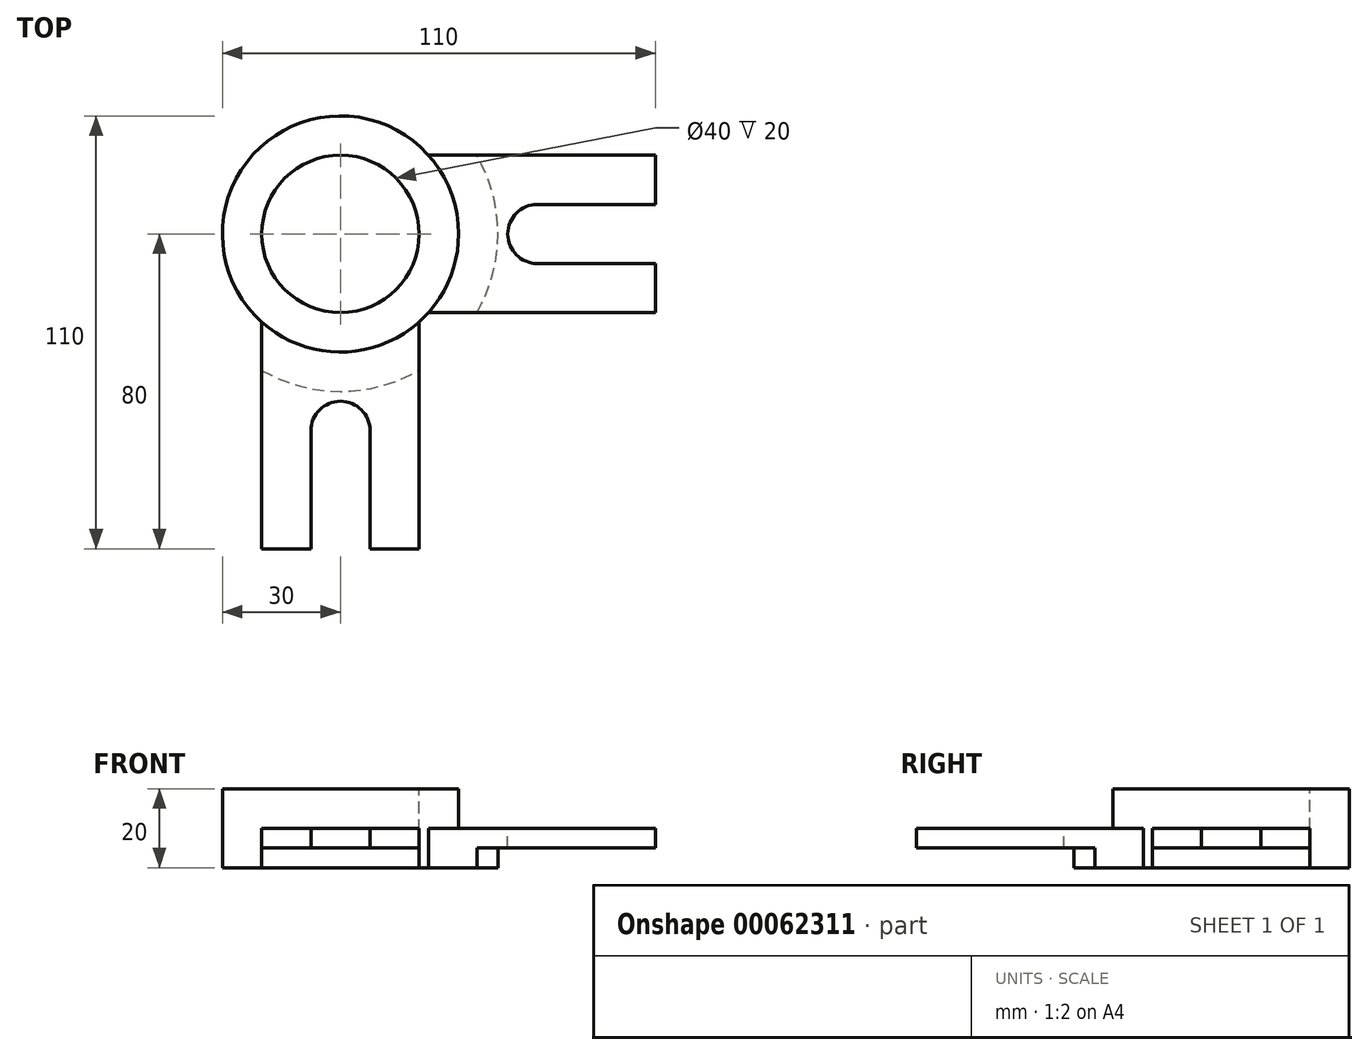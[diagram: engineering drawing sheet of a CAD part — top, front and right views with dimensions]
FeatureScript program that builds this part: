
annotation { "Feature Type Name" : "Feature", "Feature Type Description" : "" }
export const myFeature = defineFeature(function(context is Context, id is Id, definition is map)
    precondition{}
    {
        {
            var Q0;
            Q0=qCreatedBy(makeId("Top.planeOp"),FACE);
            var sketch = newSketch(context, id + "F0", { "sketchPlane" : qUnion([Q0])});
            skCircle(sketch, "E0", {"center": v(0, 0) * mm, "radius": 30 * mm});
            skSolve(sketch);
        }
        {
            var Q0;
            Q0=makeQuery(id+"F0.imprint","IMPRINT",FACE,{"disambiguationData":[TD([[makeQuery(id+"F0.imprint","IMPRINT",EDGE,{"derivedFrom":sQuery(id+"F0.wireOp",EDGE,"E0")}),1.0]])]});
            extrude(context, id + "F1", {"entities" : qUnion([Q0]), "depth" : 20 * mm});
        }
        {
            var Q0;
            Q0=qCreatedBy(makeId("Top.planeOp"),FACE);
            var sketch = newSketch(context, id + "F2", { "sketchPlane" : qUnion([Q0])});
            skLineSegment(sketch, "E1.bottom", {"start": v(22.36, -20) * mm, "end": v(80, -20) * mm});
            skLineSegment(sketch, "E1.top", {"start": v(22.36, 20) * mm, "end": v(80, 20) * mm});
            skLineSegment(sketch, "E1.right", {"start": v(80, -20) * mm, "end": v(80, 20) * mm});
            skLineSegment(sketch, "E2.top", {"start": v(-20, -80) * mm, "end": v(20, -80) * mm});
            skLineSegment(sketch, "E2.left", {"start": v(-20, -22.36) * mm, "end": v(-20, -80) * mm});
            skArc(sketch, "E3", {"start": v(-20, -22.36) * mm, "mid": v(21.21, -21.21) * mm, "end": v(22.36, 20) * mm});
            skLineSegment(sketch, "E4.trimOffspring", {"start": v(20, -22.36) * mm, "end": v(20, -80) * mm});
            skSolve(sketch);
        }
        {
            var Q0;
            {var subQ0=sQuery(id+"F2.wireOp",EDGE,"E1.bottom");Q0=makeQuery(id+"F2.imprint","IMPRINT",FACE,{"disambiguationData":[TD([[makeQuery(id+"F2.imprint","IMPRINT",EDGE,{"derivedFrom":subQ0}),1.0]])]});}
            var Q1;
            Q1=makeQuery(id+"F2.imprint","IMPRINT",FACE,{"disambiguationData":[TD([[makeQuery(id+"F2.imprint","IMPRINT",EDGE,{"derivedFrom":sQuery(id+"F2.wireOp",EDGE,"E2.top")}),1.0]])]});
            extrude(context, id + "F3", {"entities" : qUnion([Q0, Q1]), "operationType" : NewBodyOperationType.ADD, "depth" : 10 * mm});
        }
        {
            var Q0;
            Q0=makeQuery(id+"F3.opExtrude","CAP_FACE",FACE,{"disambiguationData":[OSD([sQuery(id+"F2.wireOp",EDGE,"E2.top"),sQuery(id+"F2.wireOp",EDGE,"E2.left"),sQuery(id+"F2.wireOp",EDGE,"E3"),sQuery(id+"F2.wireOp",EDGE,"E4.trimOffspring")])],"isStart":false});
            var sketch = newSketch(context, id + "F4", { "sketchPlane" : qUnion([Q0])});
            skArc(sketch, "E5", {"start": v(7.5, -50) * mm, "mid": v(0, -42.5) * mm, "end": v(-7.5, -50) * mm});
            skPoint(sketch, "E5.centerSnap0", {"position": v(0, -80) * mm});
            skLineSegment(sketch, "E6.3", {"start": v(-25, -85) * mm, "end": v(25, -85) * mm});
            skLineSegment(sketch, "E7.0", {"start": v(7.5, -50) * mm, "end": v(7.5, -80) * mm});
            skLineSegment(sketch, "E8.0", {"start": v(-7.5, -50) * mm, "end": v(-7.5, -80) * mm});
            skLineSegment(sketch, "E9", {"start": v(-7.5, -80) * mm, "end": v(7.5, -80) * mm});
            skSolve(sketch);
        }
        {
            var Q0;
            Q0=makeQuery(id+"F4.imprint","IMPRINT",FACE,{"disambiguationData":[TD([[makeQuery(id+"F4.imprint","IMPRINT",EDGE,{"derivedFrom":sQuery(id+"F4.wireOp",EDGE,"E5")}),1.0]])]});
            extrude(context, id + "F5", {"entities" : qUnion([Q0]), "operationType" : NewBodyOperationType.REMOVE, "oppositeDirection" : true, "depth" : 25 * mm});
        }
        {
            var Q0;
            Q0=makeQuery(id+"F3.opExtrude","CAP_FACE",FACE,{"disambiguationData":[OSD([sQuery(id+"F2.wireOp",EDGE,"E1.bottom"),sQuery(id+"F2.wireOp",EDGE,"E1.top"),sQuery(id+"F2.wireOp",EDGE,"E1.right"),sQuery(id+"F2.wireOp",EDGE,"E3")])],"isStart":false});
            var sketch = newSketch(context, id + "F6", { "sketchPlane" : qUnion([Q0])});
            skArc(sketch, "E10", {"start": v(50, 7.5) * mm, "mid": v(42.5, 0) * mm, "end": v(50, -7.5) * mm});
            skLineSegment(sketch, "E11.0", {"start": v(50, 7.5) * mm, "end": v(80, 7.5) * mm});
            skLineSegment(sketch, "E12.0", {"start": v(50, -7.5) * mm, "end": v(80, -7.5) * mm});
            skLineSegment(sketch, "E13", {"start": v(80, 7.5) * mm, "end": v(80, -7.5) * mm});
            skSolve(sketch);
        }
        {
            var Q0;
            Q0=makeQuery(id+"F6.imprint","IMPRINT",FACE,{"disambiguationData":[TD([[makeQuery(id+"F6.imprint","IMPRINT",EDGE,{"derivedFrom":sQuery(id+"F6.wireOp",EDGE,"E10")}),1.0]])]});
            extrude(context, id + "F7", {"entities" : qUnion([Q0]), "operationType" : NewBodyOperationType.REMOVE, "oppositeDirection" : true, "depth" : 10 * mm});
        }
        {
            var Q0;
            Q0=qCreatedBy(makeId("Top.planeOp"),FACE);
            var sketch = newSketch(context, id + "F8", { "sketchPlane" : qUnion([Q0])});
            skArc(sketch, "E14", {"start": v(-20, -34.64) * mm, "mid": v(0, -40) * mm, "end": v(20, -34.64) * mm});
            skLineSegment(sketch, "E15.top", {"start": v(-20, -80) * mm, "end": v(20, -80) * mm});
            skLineSegment(sketch, "E15.left", {"start": v(-20, -34.64) * mm, "end": v(-20, -80) * mm});
            skLineSegment(sketch, "E15.right", {"start": v(20, -34.64) * mm, "end": v(20, -80) * mm});
            skLineSegment(sketch, "E16.bottom", {"start": v(34.45, -20) * mm, "end": v(80, -20) * mm});
            skLineSegment(sketch, "E16.top", {"start": v(34.41, 20) * mm, "end": v(80, 20) * mm});
            skLineSegment(sketch, "E16.right", {"start": v(80, -20) * mm, "end": v(80, 20) * mm});
            skArc(sketch, "E17.trimOffspring", {"start": v(34.64, -20) * mm, "mid": v(40, 0) * mm, "end": v(34.64, 20) * mm});
            skSolve(sketch);
        }
        {
            var Q0;
            Q0=makeQuery(id+"F8.imprint","IMPRINT",FACE,{"disambiguationData":[TD([[makeQuery(id+"F8.imprint","IMPRINT",EDGE,{"derivedFrom":sQuery(id+"F8.wireOp",EDGE,"E14")}),-1.0]])]});
            var Q1;
            {var subQ0=sQuery(id+"F8.wireOp",EDGE,"E16.right");Q1=makeQuery(id+"F8.imprint","IMPRINT",FACE,{"disambiguationData":[TD([[makeQuery(id+"F8.imprint","IMPRINT",EDGE,{"derivedFrom":subQ0}),1.0]])]});}
            extrude(context, id + "F9", {"entities" : qUnion([Q0, Q1]), "operationType" : NewBodyOperationType.REMOVE, "depth" : 5 * mm});
        }
        {
            var Q0;
            Q0=makeQuery(id+"F1.opExtrude","CAP_FACE",FACE,{"disambiguationData":[OSD([sQuery(id+"F0.wireOp",EDGE,"E0")])],"isStart":false});
            var sketch = newSketch(context, id + "F10", { "sketchPlane" : qUnion([Q0])});
            skCircle(sketch, "E18", {"center": v(0, 0) * mm, "radius": 20 * mm});
            skSolve(sketch);
        }
        {
            var Q0;
            Q0=makeQuery(id+"F10.imprint","IMPRINT",FACE,{"disambiguationData":[TD([[makeQuery(id+"F10.imprint","IMPRINT",EDGE,{"derivedFrom":sQuery(id+"F10.wireOp",EDGE,"E18")}),1.0]])]});
            extrude(context, id + "F11", {"entities" : qUnion([Q0]), "operationType" : NewBodyOperationType.REMOVE, "oppositeDirection" : true, "depth" : 20 * mm});
        }
    });
